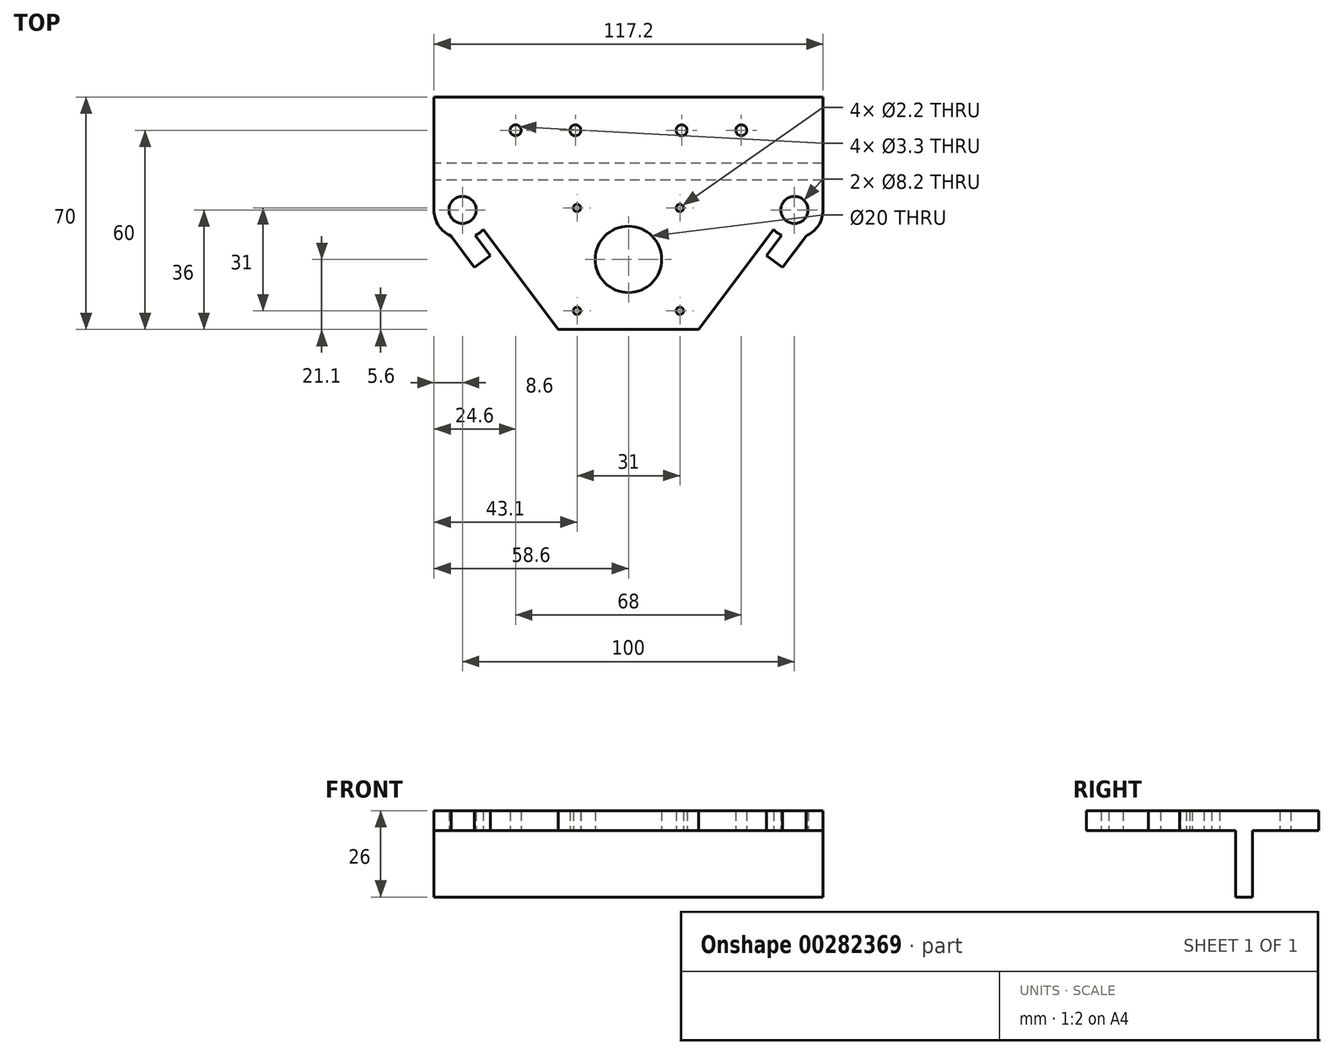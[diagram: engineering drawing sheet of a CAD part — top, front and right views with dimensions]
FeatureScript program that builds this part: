
annotation { "Feature Type Name" : "Feature", "Feature Type Description" : "" }
export const myFeature = defineFeature(function(context is Context, id is Id, definition is map)
    precondition{}
    {
        {
            var Q0;
            Q0=qCreatedBy(makeId("Top.planeOp"),FACE);
            var sketch = newSketch(context, id + "F0", { "sketchPlane" : qUnion([Q0])});
            skLineSegment(sketch, "E0.bottom", {"start": v(0, 0) * mm, "end": v(0, 0) * mm});
            skLineSegment(sketch, "E0.top", {"start": v(0, 25) * mm, "end": v(0, 25) * mm});
            skLineSegment(sketch, "E0.left", {"start": v(0, 0) * mm, "end": v(0, 25) * mm});
            skLineSegment(sketch, "E0.right", {"start": v(0, -9) * mm, "end": v(0, 25) * mm});
            skLineSegment(sketch, "E1", {"start": v(0, 25) * mm, "end": v(117.2, 25) * mm});
            skLineSegment(sketch, "E2", {"start": v(117.2, 25) * mm, "end": v(117.2, -9) * mm});
            skLineSegment(sketch, "E3", {"start": v(37.5, -45) * mm, "end": v(79.7, -45) * mm});
            skLineSegment(sketch, "E4", {"start": v(58.6, 25) * mm, "end": v(58.6, -45) * mm, "construction": true});
            skLineSegment(sketch, "E5.bottom", {"start": v(74.1, -39.4) * mm, "end": v(43.1, -39.4) * mm, "construction": true});
            skLineSegment(sketch, "E5.top", {"start": v(74.1, -8.4) * mm, "end": v(43.1, -8.4) * mm, "construction": true});
            skLineSegment(sketch, "E5.left", {"start": v(74.1, -39.4) * mm, "end": v(74.1, -8.4) * mm, "construction": true});
            skLineSegment(sketch, "E5.right", {"start": v(43.1, -39.4) * mm, "end": v(43.1, -8.4) * mm, "construction": true});
            skPoint(sketch, "E5.middle", {"position": v(58.6, -23.9) * mm});
            skCircle(sketch, "E6", {"center": v(43.1, -8.4) * mm, "radius": 1.1 * mm});
            skCircle(sketch, "E7", {"center": v(74.1, -8.4) * mm, "radius": 1.1 * mm});
            skCircle(sketch, "E8", {"center": v(74.1, -39.4) * mm, "radius": 1.1 * mm});
            skCircle(sketch, "E9", {"center": v(43.1, -39.4) * mm, "radius": 1.1 * mm});
            skCircle(sketch, "E10", {"center": v(58.6, -23.9) * mm, "radius": 10 * mm});
            skLineSegment(sketch, "E11", {"start": v(0, 15) * mm, "end": v(117.2, 15) * mm, "construction": true});
            skCircle(sketch, "E12", {"center": v(42.6, 15) * mm, "radius": 1.65 * mm});
            skCircle(sketch, "E13", {"center": v(24.6, 15) * mm, "radius": 1.65 * mm});
            skCircle(sketch, "E14", {"center": v(74.6, 15) * mm, "radius": 1.65 * mm});
            skCircle(sketch, "E15", {"center": v(92.6, 15) * mm, "radius": 1.65 * mm});
            skLineSegment(sketch, "E16.bottom", {"start": v(79.7, -2.8) * mm, "end": v(37.5, -2.8) * mm, "construction": true});
            skLineSegment(sketch, "E16.top", {"start": v(79.7, -45) * mm, "end": v(37.5, -45) * mm, "construction": true});
            skLineSegment(sketch, "E16.left", {"start": v(79.7, -2.8) * mm, "end": v(79.7, -45) * mm, "construction": true});
            skLineSegment(sketch, "E16.right", {"start": v(37.5, -2.8) * mm, "end": v(37.5, -45) * mm, "construction": true});
            skLineSegment(sketch, "E17", {"start": v(8.6, 15) * mm, "end": v(8.6, -9) * mm, "construction": true});
            skLineSegment(sketch, "E18", {"start": v(108.6, 15) * mm, "end": v(108.6, -9) * mm, "construction": true});
            skLineSegment(sketch, "E19", {"start": v(8.6, -9) * mm, "end": v(37.5, -47.5) * mm, "construction": true});
            skLineSegment(sketch, "E20", {"start": v(108.6, -9) * mm, "end": v(79.7, -47.5) * mm, "construction": true});
            skCircle(sketch, "E21", {"center": v(8.6, -9) * mm, "radius": 4.1 * mm});
            skCircle(sketch, "E22", {"center": v(108.6, -9) * mm, "radius": 4.1 * mm});
            skLineSegment(sketch, "E23", {"start": v(37.5, -45) * mm, "end": v(36.3, -45.9) * mm, "construction": true});
            skLineSegment(sketch, "E24", {"start": v(79.7, -45) * mm, "end": v(80.9, -45.9) * mm, "construction": true});
            skCircle(sketch, "E25", {"center": v(8.6, -9) * mm, "radius": 8.6 * mm});
            skCircle(sketch, "E26", {"center": v(108.6, -9) * mm, "radius": 8.6 * mm});
            skLineSegment(sketch, "E27.0", {"start": v(9.8, -8.1) * mm, "end": v(38.2, -45.93) * mm});
            skLineSegment(sketch, "E28.0", {"start": v(7.4, -9.9) * mm, "end": v(35.8, -47.74) * mm});
            skLineSegment(sketch, "E29.0", {"start": v(2.6, -13.5) * mm, "end": v(31, -51.34) * mm});
            skLineSegment(sketch, "E30.0", {"start": v(107.12, -8.47) * mm, "end": v(78.72, -46.3) * mm});
            skLineSegment(sketch, "E31.0", {"start": v(109.52, -10.27) * mm, "end": v(81.12, -48.1) * mm});
            skLineSegment(sketch, "E32.0", {"start": v(114.32, -13.87) * mm, "end": v(85.92, -51.7) * mm});
            skLineSegment(sketch, "E33", {"start": v(8.6, -9) * mm, "end": v(0, -9) * mm, "construction": true});
            skLineSegment(sketch, "E34", {"start": v(108.6, -9) * mm, "end": v(117.2, -9) * mm, "construction": true});
            skLineSegment(sketch, "E35", {"start": v(17, -22.7) * mm, "end": v(12.2, -26.3) * mm});
            skLineSegment(sketch, "E36", {"start": v(100.2, -22.7) * mm, "end": v(105, -26.3) * mm});
            skSolve(sketch);
        }
        {
            var Q0;
            Q0 = qSketchRegion(id + "F0", true);
            extrude(context, id + "F1", {"entities" : qUnion([Q0]), "depth" : 6 * mm});
        }
        {
            var Q0;
            Q0=qCreatedBy(makeId("Right.planeOp"),FACE);
            var sketch = newSketch(context, id + "F2", { "sketchPlane" : qUnion([Q0])});
            skLineSegment(sketch, "E37.bottom", {"start": v(0, 0) * mm, "end": v(5, 0) * mm});
            skLineSegment(sketch, "E37.top", {"start": v(0, -20) * mm, "end": v(5, -20) * mm});
            skLineSegment(sketch, "E37.left", {"start": v(0, 0) * mm, "end": v(0, -20) * mm});
            skLineSegment(sketch, "E37.right", {"start": v(5, 0) * mm, "end": v(5, -20) * mm});
            skSolve(sketch);
        }
        {
            var Q0;
            Q0 = qSketchRegion(id + "F2", true);
            extrude(context, id + "F3", {"entities" : qUnion([Q0]), "operationType" : NewBodyOperationType.ADD, "depth" : 117.2 * mm});
        }
    });
